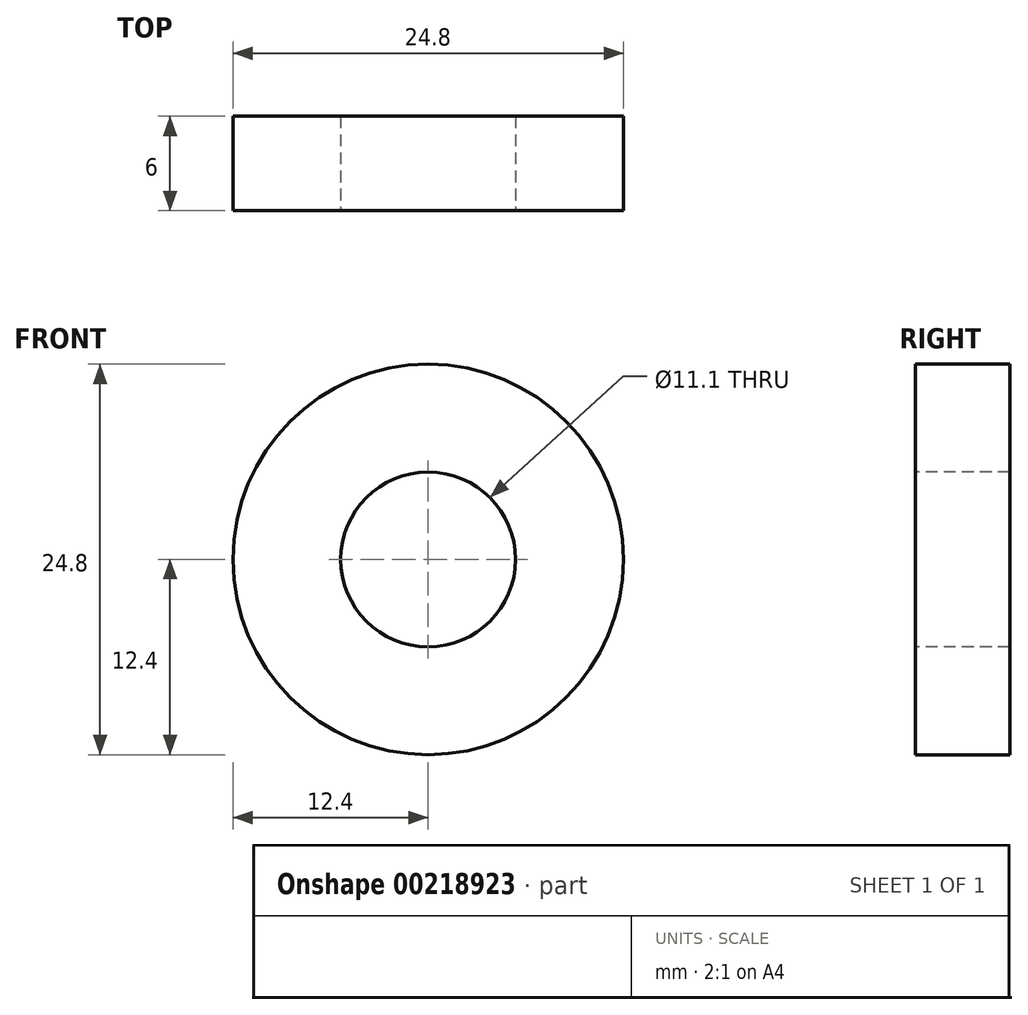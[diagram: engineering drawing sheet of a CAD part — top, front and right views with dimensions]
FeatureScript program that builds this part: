
annotation { "Feature Type Name" : "Feature", "Feature Type Description" : "" }
export const myFeature = defineFeature(function(context is Context, id is Id, definition is map)
    precondition{}
    {
        {
            var Q0;
            Q0=qCreatedBy(makeId("Front.planeOp"),FACE);
            var sketch = newSketch(context, id + "F0", { "sketchPlane" : qUnion([Q0])});
            skCircle(sketch, "E0", {"center": v(0, 0) * mm, "radius": 12.4 * mm});
            skSolve(sketch);
        }
        {
            var Q0;
            Q0=qSketchRegion(id+"F0",true);
            extrude(context, id + "F1", {"entities" : qUnion([Q0]), "depth" : 6 * mm});
        }
        {
            var Q0;
            Q0=makeQuery(id+"F1.opExtrude","CAP_FACE",FACE,{"disambiguationData":[OSD([sQuery(id+"F0.wireOp",EDGE,"E0")])],"isStart":false});
            var sketch = newSketch(context, id + "F2", { "sketchPlane" : qUnion([Q0])});
            skCircle(sketch, "E1", {"center": v(0, 0) * mm, "radius": 5.55 * mm});
            skSolve(sketch);
        }
        {
            var Q0;
            Q0 = qSketchRegion(id + "F2", true);
            extrude(context, id + "F3", {"entities" : qUnion([Q0]), "operationType" : NewBodyOperationType.REMOVE, "oppositeDirection" : true, "depth" : 25 * mm});
        }
    });
